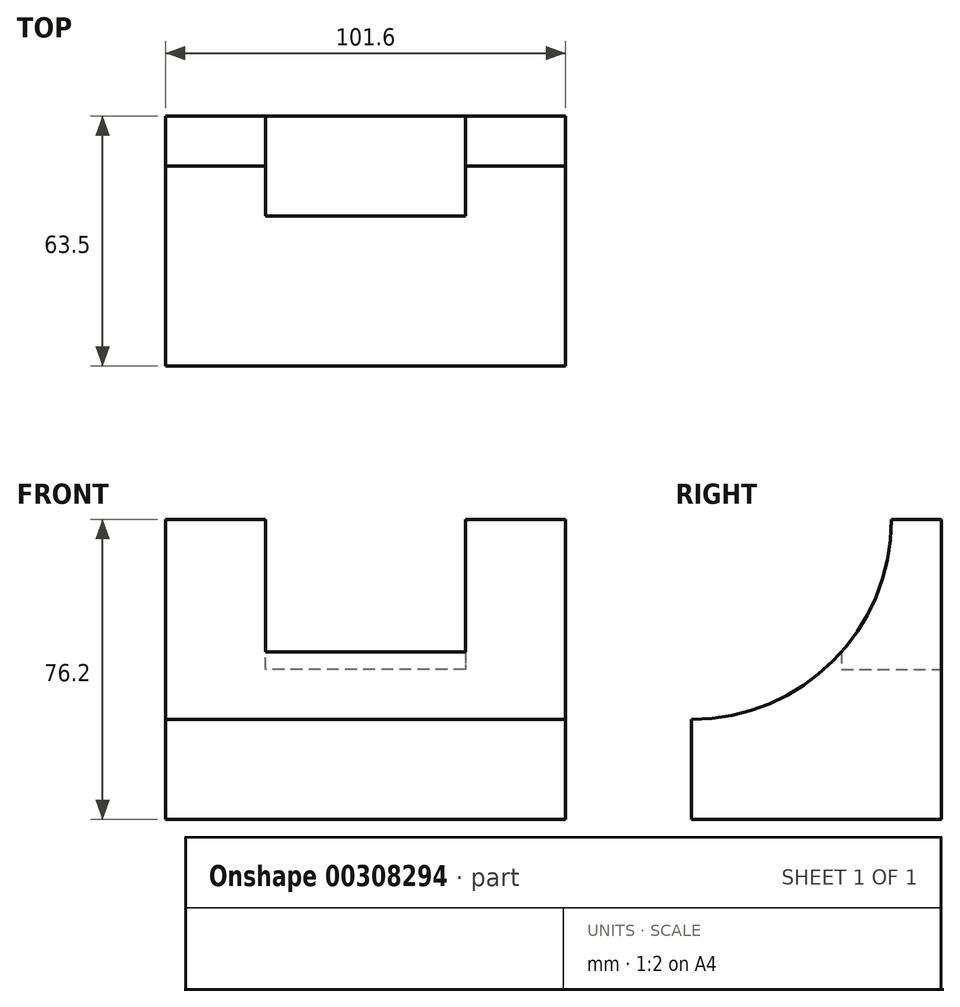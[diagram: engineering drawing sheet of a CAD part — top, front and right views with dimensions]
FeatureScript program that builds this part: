
annotation { "Feature Type Name" : "Feature", "Feature Type Description" : "" }
export const myFeature = defineFeature(function(context is Context, id is Id, definition is map)
    precondition{}
    {
        {
            var Q0;
            Q0=qCreatedBy(makeId("Front.planeOp"),FACE);
            var sketch = newSketch(context, id + "F0", { "sketchPlane" : qUnion([Q0])});
            skLineSegment(sketch, "E0", {"start": v(-55.3, 25.88) * mm, "end": v(-55.3, -50.32) * mm});
            skLineSegment(sketch, "E1", {"start": v(-55.3, -50.32) * mm, "end": v(46.3, -50.32) * mm});
            skLineSegment(sketch, "E2", {"start": v(46.3, -50.32) * mm, "end": v(46.3, 25.88) * mm});
            skLineSegment(sketch, "E3", {"start": v(46.3, 25.88) * mm, "end": v(-55.3, 25.88) * mm});
            skSolve(sketch);
        }
        {
            var Q0;
            Q0=makeQuery(id+"F0.imprint","IMPRINT",FACE,{"disambiguationData":[TD([[makeQuery(id+"F0.imprint","IMPRINT",EDGE,{"derivedFrom":sQuery(id+"F0.wireOp",EDGE,"E0")}),1.0]])]});
            extrude(context, id + "F1", {"entities" : qUnion([Q0]), "depth" : 63.5 * mm});
        }
        {
            var Q0;
            Q0=makeQuery(id+"F1.opExtrude","SWEPT_FACE",FACE,{"disambiguationData":[OSD([sQuery(id+"F0.wireOp",EDGE,"E2")])]});
            var sketch = newSketch(context, id + "F2", { "sketchPlane" : qUnion([Q0])});
            skArc(sketch, "E4", {"start": v(-63.5, -24.92) * mm, "mid": v(-27.58, -10.04) * mm, "end": v(-12.7, 25.88) * mm});
            skLineSegment(sketch, "E5", {"start": v(0, 25.88) * mm, "end": v(-63.5, 25.88) * mm});
            skLineSegment(sketch, "E6", {"start": v(-63.5, -50.32) * mm, "end": v(-63.5, 25.88) * mm});
            skSolve(sketch);
        }
        {
            var Q0;
            {var subQ0=sQuery(id+"F2.wireOp",EDGE,"E4");Q0=makeQuery(id+"F2.imprint","IMPRINT",FACE,{"disambiguationData":[TD([[makeQuery(id+"F2.imprint","IMPRINT",EDGE,{"derivedFrom":subQ0}),1.0]])]});}
            extrude(context, id + "F3", {"entities" : qUnion([Q0]), "operationType" : NewBodyOperationType.REMOVE, "oppositeDirection" : true, "depth" : 114.3 * mm});
        }
        {
            var Q0;
            Q0=makeQuery(id+"F1.opExtrude","CAP_FACE",FACE,{"disambiguationData":[OSD([sQuery(id+"F0.wireOp",EDGE,"E0"),sQuery(id+"F0.wireOp",EDGE,"E1"),sQuery(id+"F0.wireOp",EDGE,"E2"),sQuery(id+"F0.wireOp",EDGE,"E3")])],"isStart":true});
            var sketch = newSketch(context, id + "F4", { "sketchPlane" : qUnion([Q0])});
            skLineSegment(sketch, "E7", {"start": v(-20.9, 25.88) * mm, "end": v(-20.9, -12.22) * mm});
            skLineSegment(sketch, "E8", {"start": v(-20.9, -12.22) * mm, "end": v(29.9, -12.22) * mm});
            skLineSegment(sketch, "E9", {"start": v(29.9, -12.22) * mm, "end": v(29.9, 25.88) * mm});
            skLineSegment(sketch, "E10", {"start": v(-46.3, 25.88) * mm, "end": v(-20.9, 25.88) * mm});
            skLineSegment(sketch, "E11", {"start": v(29.9, 25.88) * mm, "end": v(55.3, 25.88) * mm});
            skSolve(sketch);
        }
        {
            var Q0;
            Q0 = qSketchRegion(id + "F4", true);
            var Q1;
            {var subQ0=sQuery(id+"F4.wireOp",EDGE,"E7");Q1=makeQuery(id+"F4.imprint","IMPRINT",FACE,{"disambiguationData":[TD([[makeQuery(id+"F4.imprint","IMPRINT",EDGE,{"derivedFrom":subQ0}),1.0]])]});}
            extrude(context, id + "F5", {"entities" : qUnion([Q0, Q1]), "operationType" : NewBodyOperationType.REMOVE, "oppositeDirection" : true, "depth" : 25.4 * mm});
        }
    });
